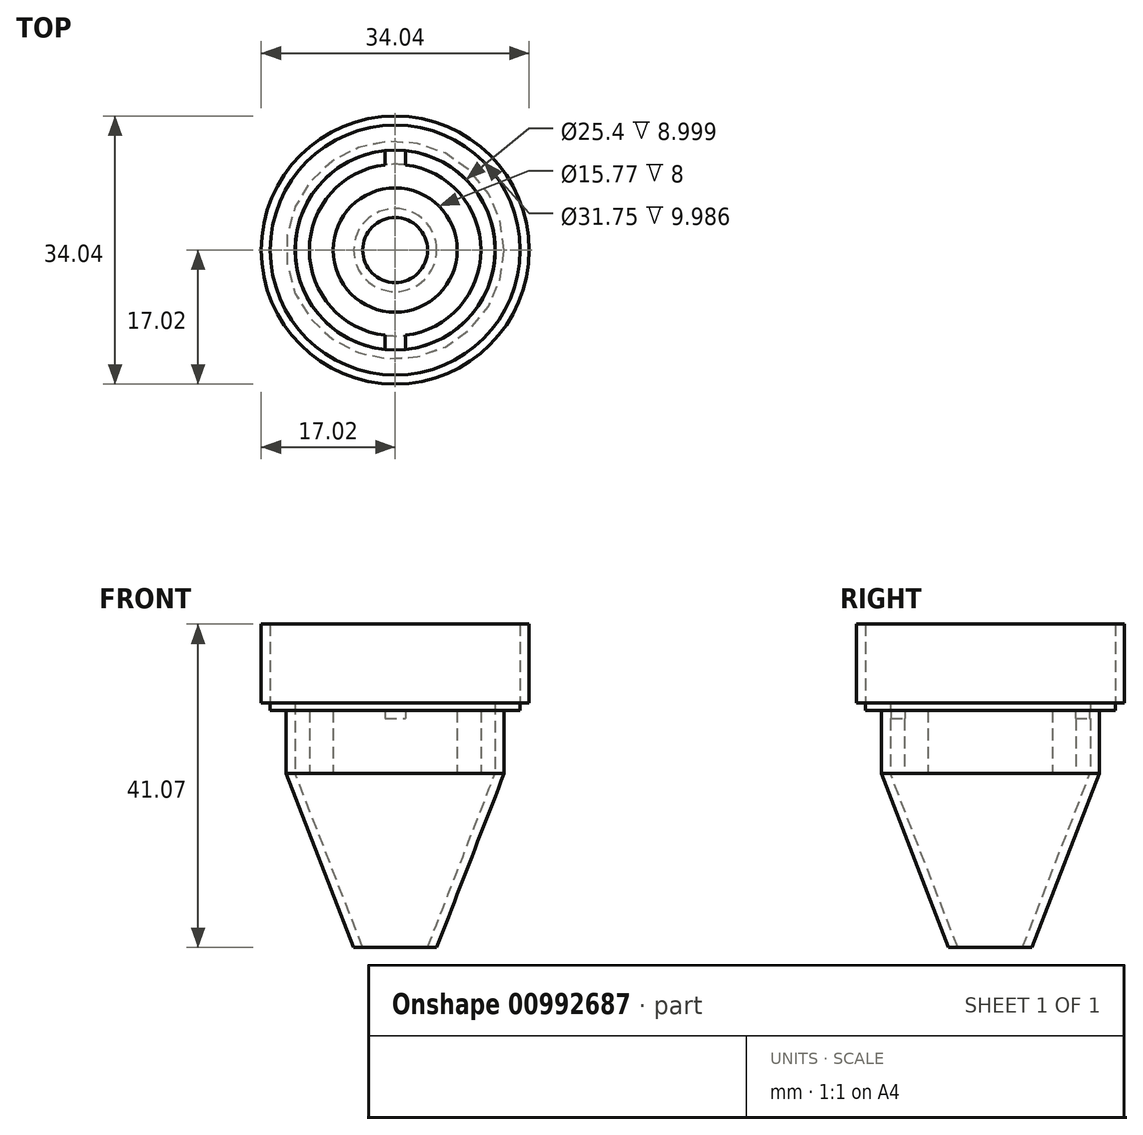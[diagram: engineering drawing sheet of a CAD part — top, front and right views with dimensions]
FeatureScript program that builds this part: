
annotation { "Feature Type Name" : "Feature", "Feature Type Description" : "" }
export const myFeature = defineFeature(function(context is Context, id is Id, definition is map)
    precondition{}
    {
        {
            var Q0;
            Q0=qCreatedBy(makeId("Top.planeOp"),FACE);
            var sketch = newSketch(context, id + "F0", { "sketchPlane" : qUnion([Q0])});
            skCircle(sketch, "E0", {"center": v(0, 0) * mm, "radius": 7.89 * mm});
            skArc(sketch, "E1", {"start": v(1.3, -10.82) * mm, "mid": v(10.9, 0) * mm, "end": v(1.3, 10.82) * mm});
            skArc(sketch, "E2", {"start": v(1.3, -12.63) * mm, "mid": v(12.7, 0) * mm, "end": v(1.3, 12.63) * mm});
            skCircle(sketch, "E3", {"center": v(0, 0) * mm, "radius": 13.84 * mm});
            skLineSegment(sketch, "E4", {"start": v(-1.3, -12.63) * mm, "end": v(-1.3, -10.82) * mm});
            skLineSegment(sketch, "E5.MirrorCS", {"start": v(1.3, -12.63) * mm, "end": v(1.3, -10.82) * mm});
            skLineSegment(sketch, "E6.trimOffspring", {"start": v(-1.3, 10.82) * mm, "end": v(-1.3, 12.63) * mm});
            skLineSegment(sketch, "E7.trimOffspring", {"start": v(1.3, 10.82) * mm, "end": v(1.3, 12.63) * mm});
            skArc(sketch, "E8.trimOffspring", {"start": v(-1.3, 10.82) * mm, "mid": v(-10.9, 0) * mm, "end": v(-1.3, -10.82) * mm});
            skArc(sketch, "E9.trimOffspring", {"start": v(-1.3, 12.63) * mm, "mid": v(-12.7, 0) * mm, "end": v(-1.3, -12.63) * mm});
            skSolve(sketch);
        }
        {
            var Q0;
            Q0=qSketchRegion(id+"F0",true);
            extrude(context, id + "F1", {"entities" : qUnion([Q0]), "depth" : 8 * mm, "offsetDistance" : 25.4 * mm});
        }
        {
            var Q0;
            Q0=qCreatedBy(makeId("Top.planeOp"),FACE);
            var sketch = newSketch(context, id + "F2", { "sketchPlane" : qUnion([Q0])});
            skCircle(sketch, "E10", {"center": v(0, 0) * mm, "radius": 12.7 * mm});
            skCircle(sketch, "E11", {"center": v(0, 0) * mm, "radius": 10.9 * mm});
            skSolve(sketch);
        }
        {
            var Q0;
            Q0=qSketchRegion(id+"F2",true);
            extrude(context, id + "F3", {"entities" : qUnion([Q0]), "depth" : 7 * mm, "offsetDistance" : 25.4 * mm});
        }
        {
            var Q0;
            Q0=makeQuery(id+"F3.opExtrude","SWEPT_BODY",BODY,{"disambiguationData":[OSD([sQuery(id+"F2.wireOp",EDGE,"E10"),sQuery(id+"F2.wireOp",EDGE,"E11")])]});
            var Q1;
            Q1=makeQuery(id+"F1.opExtrude","SWEPT_BODY",BODY,{"disambiguationData":[OSD([sQuery(id+"F0.wireOp",EDGE,"E0"),sQuery(id+"F0.wireOp",EDGE,"E1"),sQuery(id+"F0.wireOp",EDGE,"E2"),sQuery(id+"F0.wireOp",EDGE,"E3"),sQuery(id+"F0.wireOp",EDGE,"E4"),sQuery(id+"F0.wireOp",EDGE,"E5.MirrorCS"),sQuery(id+"F0.wireOp",EDGE,"E6.trimOffspring"),sQuery(id+"F0.wireOp",EDGE,"E7.trimOffspring"),sQuery(id+"F0.wireOp",EDGE,"E8.trimOffspring"),sQuery(id+"F0.wireOp",EDGE,"E9.trimOffspring")])]});
            booleanBodies(context, id + "F4", {"operationType" : BooleanOperationType.SUBTRACTION, "tools" : qUnion([Q0]), "targets" : qUnion([Q1])});
        }
        {
            var Q0;
            Q0=qCreatedBy(makeId("Top.planeOp"),FACE);
            cPlane(context, id + "F5", {"entities" : qUnion([Q0]), "cplaneType" : CPlaneType.OFFSET, "offset" : 8 * mm, "width" : 152.4 * mm, "height" : 152.4 * mm});
        }
        {
            var Q0;
            Q0=qCreatedBy(id+"F5.planeOp",FACE);
            var sketch = newSketch(context, id + "F6", { "sketchPlane" : qUnion([Q0])});
            skCircle(sketch, "E12", {"center": v(0, 0) * mm, "radius": 15.88 * mm});
            skCircle(sketch, "E13", {"center": v(0, 0) * mm, "radius": 12.7 * mm});
            skSolve(sketch);
        }
        {
            var Q0;
            Q0 = qSketchRegion(id + "F6", true);
            extrude(context, id + "F7", {"entities" : qUnion([Q0]), "operationType" : NewBodyOperationType.ADD, "depth" : 1 * mm, "offsetDistance" : 25.4 * mm});
        }
        {
            var Q0;
            Q0=qCreatedBy(id+"F5.planeOp",FACE);
            cPlane(context, id + "F8", {"entities" : qUnion([Q0]), "cplaneType" : CPlaneType.OFFSET, "offset" : 0.99 * mm, "width" : 152.4 * mm, "height" : 152.4 * mm});
        }
        {
            var Q0;
            Q0=qCreatedBy(id+"F8.planeOp",FACE);
            var sketch = newSketch(context, id + "F9", { "sketchPlane" : qUnion([Q0])});
            skCircle(sketch, "E14", {"center": v(0, 0) * mm, "radius": 15.88 * mm});
            skCircle(sketch, "E15", {"center": v(0, 0) * mm, "radius": 17.02 * mm});
            skSolve(sketch);
        }
        {
            var Q0;
            Q0 = qSketchRegion(id + "F9", true);
            extrude(context, id + "F10", {"entities" : qUnion([Q0]), "operationType" : NewBodyOperationType.ADD, "depth" : 10 * mm, "offsetDistance" : 25.4 * mm});
        }
        {
            var Q0;
            Q0=qCreatedBy(makeId("Front.planeOp"),FACE);
            var sketch = newSketch(context, id + "F11", { "sketchPlane" : qUnion([Q0])});
            skLineSegment(sketch, "E16", {"start": v(-13.84, 0) * mm, "end": v(-5.28, -22.09) * mm});
            skLineSegment(sketch, "E17", {"start": v(-5.28, -22.09) * mm, "end": v(-4.13, -22.09) * mm});
            skLineSegment(sketch, "E18", {"start": v(-13.84, 0) * mm, "end": v(-12.7, 0) * mm});
            skLineSegment(sketch, "E19", {"start": v(-12.7, 0) * mm, "end": v(-4.13, -22.09) * mm});
            skLineSegment(sketch, "E20", {"start": v(0, 0) * mm, "end": v(0, -26.92) * mm});
            skSolve(sketch);
        }
        {
            var Q0;
            Q0 = qSketchRegion(id + "F11", true);
            var Q1;
            Q1=sQuery(id+"F11.wireOp",EDGE,"E20");
            revolve(context, id + "F12", {"operationType" : NewBodyOperationType.ADD, "surfaceOperationType" : NewSurfaceOperationType.NEW, "entities" : qUnion([Q0]), "axis" : qUnion([Q1]), "revolveType" : RevolveType.FULL});
        }
    });
